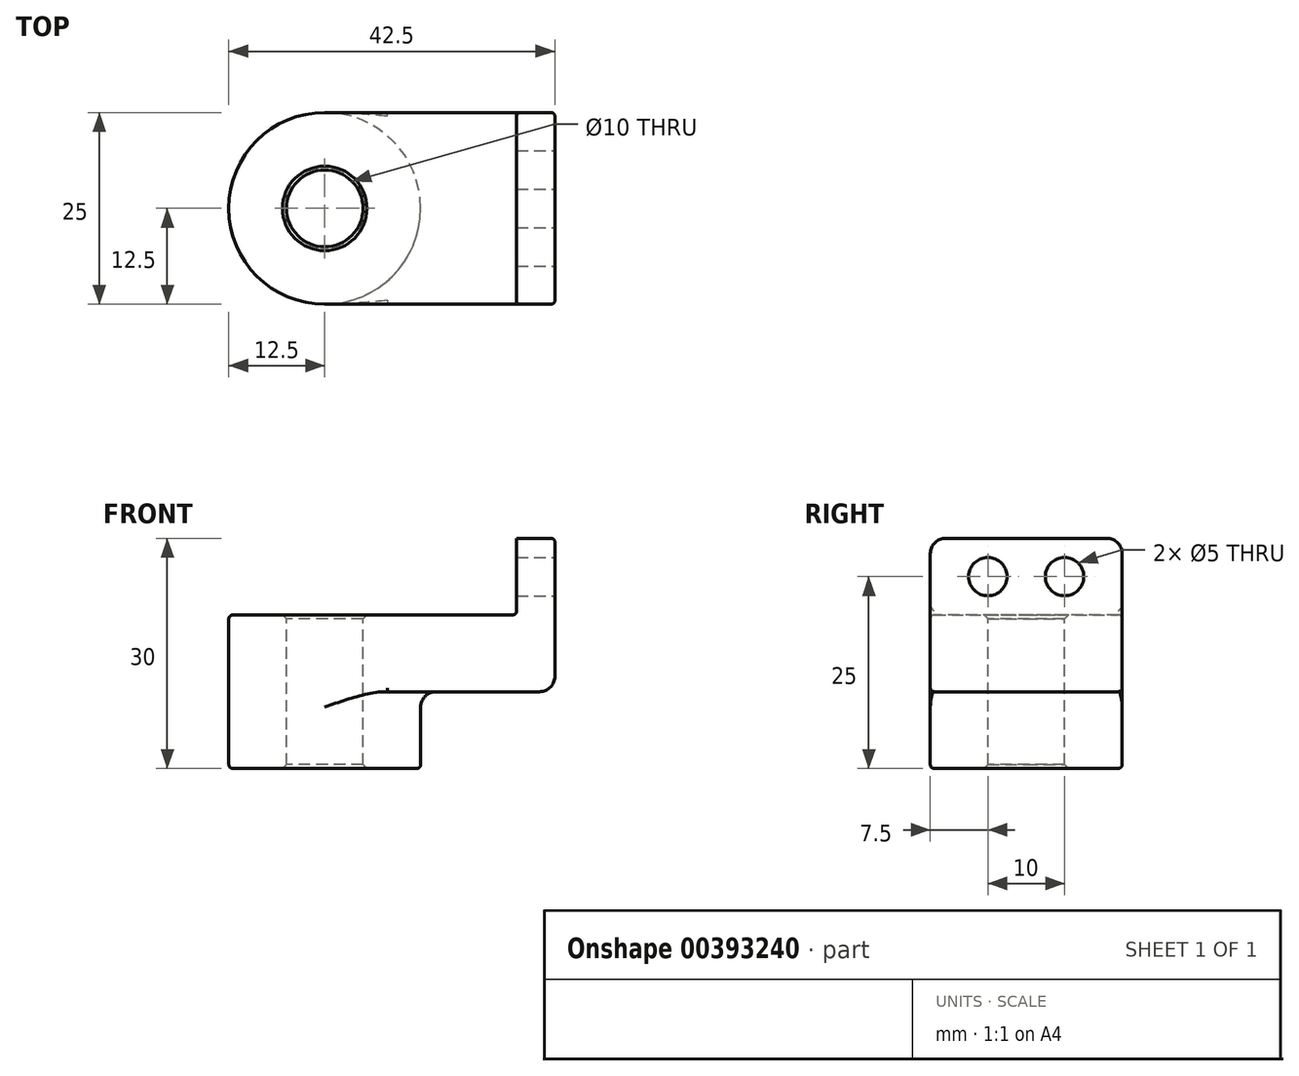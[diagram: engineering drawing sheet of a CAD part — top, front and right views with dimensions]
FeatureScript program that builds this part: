
annotation { "Feature Type Name" : "Feature", "Feature Type Description" : "" }
export const myFeature = defineFeature(function(context is Context, id is Id, definition is map)
    precondition{}
    {
        {
            var Q0;
            Q0=qCreatedBy(makeId("Top.planeOp"),FACE);
            var sketch = newSketch(context, id + "F0", { "sketchPlane" : qUnion([Q0])});
            skLineSegment(sketch, "E0.bottom", {"start": v(5.9, 12.5) * mm, "end": v(-24.1, 12.5) * mm});
            skLineSegment(sketch, "E0.top", {"start": v(5.9, -12.5) * mm, "end": v(-24.1, -12.5) * mm});
            skLineSegment(sketch, "E0.left", {"start": v(5.9, 12.5) * mm, "end": v(5.9, -12.5) * mm});
            skLineSegment(sketch, "E0.right", {"start": v(-24.1, 12.5) * mm, "end": v(-24.1, -12.5) * mm});
            skPoint(sketch, "E0.middle", {"position": v(-9.1, 0) * mm});
            skCircle(sketch, "E1", {"center": v(-24.1, 0) * mm, "radius": 12.5 * mm});
            skCircle(sketch, "E2", {"center": v(-24.1, 0) * mm, "radius": 5 * mm});
            skSolve(sketch);
        }
        {
            var Q0;
            Q0 = qSketchRegion(id + "F0", true);
            extrude(context, id + "F1", {"entities" : qUnion([Q0]), "oppositeDirection" : true, "depth" : 10 * mm});
        }
        {
            var Q0;
            {var subQ1=sQuery(id+"F0.wireOp",EDGE,"E0.right");var subQ3=sQuery(id+"F0.wireOp",EDGE,"E2");var subQ4=makeQuery(id+"F0.imprint","INTERSECT",VERTEX,{"disambiguationData":[OD(0.0)],"derivedFrom":[subQ1,subQ3]});Q0=makeQuery(id+"F0.imprint","IMPRINT",FACE,{"disambiguationData":[TD([[makeQuery(id+"F0.imprint","IMPRINT",EDGE,{"disambiguationData":[TD([[subQ4,-1.0]])],"derivedFrom":subQ3}),-1.0]])]});}
            var Q1;
            {var subQ1=sQuery(id+"F0.wireOp",EDGE,"E0.right");var subQ3=sQuery(id+"F0.wireOp",EDGE,"E2");var subQ4=makeQuery(id+"F0.imprint","INTERSECT",VERTEX,{"disambiguationData":[OD(0.0)],"derivedFrom":[subQ1,subQ3]});Q1=makeQuery(id+"F0.imprint","IMPRINT",FACE,{"disambiguationData":[TD([[makeQuery(id+"F0.imprint","IMPRINT",EDGE,{"disambiguationData":[TD([[subQ4,1.0]])],"derivedFrom":subQ3}),-1.0]])]});}
            extrude(context, id + "F2", {"entities" : qUnion([Q0, Q1]), "operationType" : NewBodyOperationType.ADD, "oppositeDirection" : true, "depth" : 20 * mm});
        }
        {
            var Q0;
            Q0=makeQuery(id+"F1.opExtrude","SWEPT_FACE",FACE,{"disambiguationData":[OSD([sQuery(id+"F0.wireOp",EDGE,"E0.left")])]});
            var sketch = newSketch(context, id + "F3", { "sketchPlane" : qUnion([Q0])});
            skLineSegment(sketch, "E3.bottom", {"start": v(12.5, -10) * mm, "end": v(-12.5, -10) * mm});
            skLineSegment(sketch, "E3.top", {"start": v(12.5, 10) * mm, "end": v(-12.5, 10) * mm});
            skLineSegment(sketch, "E3.left", {"start": v(12.5, -10) * mm, "end": v(12.5, 10) * mm});
            skLineSegment(sketch, "E3.right", {"start": v(-12.5, -10) * mm, "end": v(-12.5, 10) * mm});
            skCircle(sketch, "E4", {"center": v(5, 5) * mm, "radius": 2.5 * mm});
            skLineSegment(sketch, "E5", {"start": v(0, 0) * mm, "end": v(0, 10) * mm, "construction": true});
            skCircle(sketch, "E6.MirrorC", {"center": v(-5, 5) * mm, "radius": 2.5 * mm});
            skSolve(sketch);
        }
        {
            var Q0;
            Q0 = qSketchRegion(id + "F3", true);
            extrude(context, id + "F4", {"entities" : qUnion([Q0]), "operationType" : NewBodyOperationType.ADD, "oppositeDirection" : true, "depth" : 5 * mm});
        }
        {
            var Q0;
            {var subQ0=sQuery(id+"F0.wireOp",EDGE,"E1");Q0=makeQuery(id+"F2.boolean.opBoolean","INTERSECT",EDGE,{"derivedFrom":[makeQuery(id+"F1.opExtrude","CAP_FACE",FACE,{"disambiguationData":[OSD([sQuery(id+"F0.wireOp",EDGE,"E0.bottom"),sQuery(id+"F0.wireOp",EDGE,"E0.top"),sQuery(id+"F0.wireOp",EDGE,"E0.left"),subQ0,sQuery(id+"F0.wireOp",EDGE,"E2")])],"isStart":false}),makeQuery(id+"F2.opExtrude","SWEPT_FACE",FACE,{"disambiguationData":[OSD([subQ0])]})]});}
            var Q1;
            Q1=makeQuery(id+"F1.opExtrude","CAP_EDGE",EDGE,{"disambiguationData":[OSD([sQuery(id+"F0.wireOp",EDGE,"E0.left")])],"isStart":false});
            var Q2;
            Q2=makeQuery(id+"F4.opExtrude","SWEPT_EDGE",EDGE,{"disambiguationData":[OSD([sQuery(id+"F3.wireOp",EDGE,"E3.top"),sQuery(id+"F3.wireOp",EDGE,"E3.left")])]});
            var Q3;
            Q3=makeQuery(id+"F4.opExtrude","SWEPT_EDGE",EDGE,{"disambiguationData":[OSD([sQuery(id+"F3.wireOp",EDGE,"E3.top"),sQuery(id+"F3.wireOp",EDGE,"E3.right")])]});
            fillet(context, id + "F5", {"entities" : qUnion([Q0, Q1, Q2, Q3]), "radius" : 2 * mm, "tangentPropagation" : true, "allowEdgeOverflow" : false});
        }
        {
            var Q0;
            Q0=makeQuery(id+"F1.opExtrude","CAP_EDGE",EDGE,{"disambiguationData":[OSD([sQuery(id+"F0.wireOp",EDGE,"E0.bottom")])],"isStart":false});
            var Q1;
            Q1=makeQuery(id+"F1.opExtrude","CAP_EDGE",EDGE,{"disambiguationData":[OSD([sQuery(id+"F0.wireOp",EDGE,"E0.bottom")])],"isStart":true});
            var Q2;
            Q2=makeQuery(id+"F4.boolean.opBoolean","INTERSECT",EDGE,{"derivedFrom":[makeQuery(id+"F1.opExtrude","CAP_FACE",FACE,{"disambiguationData":[OSD([sQuery(id+"F0.wireOp",EDGE,"E0.bottom"),sQuery(id+"F0.wireOp",EDGE,"E0.top"),sQuery(id+"F0.wireOp",EDGE,"E0.left"),sQuery(id+"F0.wireOp",EDGE,"E1"),sQuery(id+"F0.wireOp",EDGE,"E2")])],"isStart":true}),makeQuery(id+"F4.opExtrude","CAP_FACE",FACE,{"disambiguationData":[OSD([sQuery(id+"F3.wireOp",EDGE,"E3.bottom"),sQuery(id+"F3.wireOp",EDGE,"E3.top"),sQuery(id+"F3.wireOp",EDGE,"E3.left"),sQuery(id+"F3.wireOp",EDGE,"E3.right"),sQuery(id+"F3.wireOp",EDGE,"E4"),sQuery(id+"F3.wireOp",EDGE,"E6.MirrorC")])],"isStart":false})]});
            fillet(context, id + "F6", {"entities" : qUnion([Q0, Q1, Q2]), "radius" : 0.5 * mm, "tangentPropagation" : true, "allowEdgeOverflow" : false});
        }
        {
            var Q0;
            {var subQ0=sQuery(id+"F0.wireOp",EDGE,"E2");Q0=makeQuery(id+"F2.boolean.opBoolean","MERGE",FACE,{"derivedFrom":[makeQuery(id+"F1.opExtrude","SWEPT_FACE",FACE,{"disambiguationData":[OSD([subQ0])]}),makeQuery(id+"F2.opExtrude","SWEPT_FACE",FACE,{"disambiguationData":[OSD([subQ0])]})]});}
            chamfer(context, id + "F7", {"entities" : qUnion([Q0]), "width" : 0.5 * mm, "tangentPropagation" : true});
        }
        {
            var Q0;
            Q0=makeQuery(id+"F2.opExtrude","CAP_EDGE",EDGE,{"disambiguationData":[OSD([sQuery(id+"F0.wireOp",EDGE,"E1")])],"isStart":false});
            fillet(context, id + "F8", {"entities" : qUnion([Q0]), "radius" : 0.5 * mm, "tangentPropagation" : true, "allowEdgeOverflow" : false});
        }
    });
